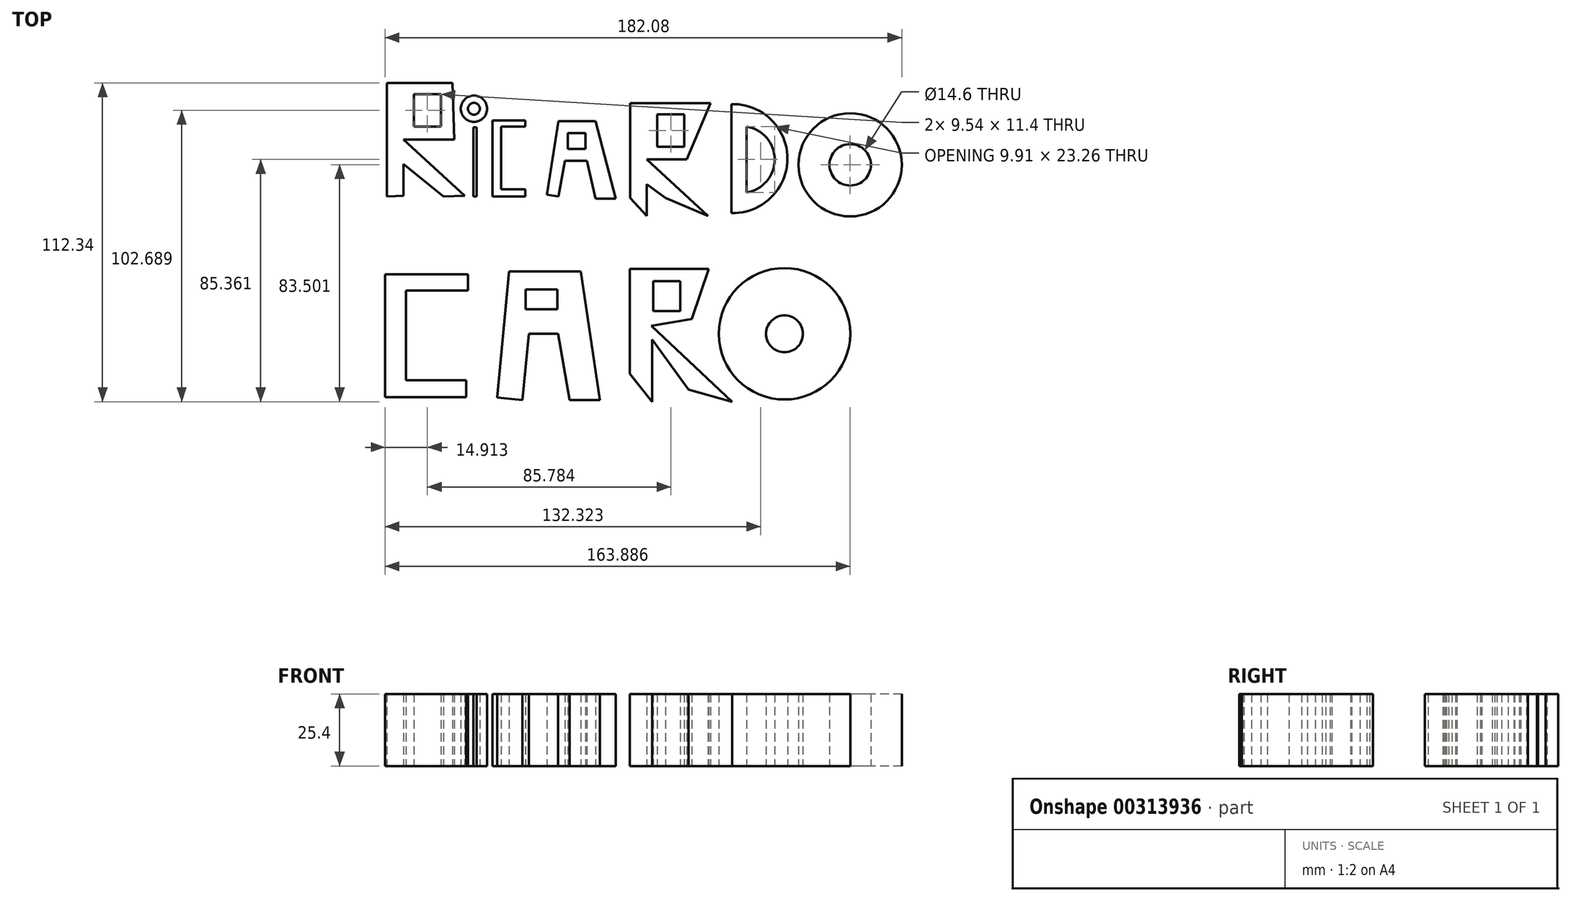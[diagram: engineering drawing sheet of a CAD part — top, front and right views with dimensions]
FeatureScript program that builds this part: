
annotation { "Feature Type Name" : "Feature", "Feature Type Description" : "" }
export const myFeature = defineFeature(function(context is Context, id is Id, definition is map)
    precondition{}
    {
        {
            var Q0;
            Q0=qCreatedBy(makeId("Top.planeOp"),FACE);
            var sketch = newSketch(context, id + "F0", { "sketchPlane" : qUnion([Q0])});
            skLineSegment(sketch, "E0", {"start": v(-68.38, 50.47) * mm, "end": v(-68.38, 10.47) * mm});
            skLineSegment(sketch, "E1", {"start": v(-68.38, 50.47) * mm, "end": v(-62.57, 50.47) * mm});
            skLineSegment(sketch, "E2", {"start": v(-62.57, 50.47) * mm, "end": v(-62.57, 10.7) * mm});
            skLineSegment(sketch, "E3", {"start": v(-68.38, 10.47) * mm, "end": v(-62.57, 10.7) * mm});
            skLineSegment(sketch, "E4", {"start": v(-62.57, 30.59) * mm, "end": v(-40.94, 10.7) * mm});
            skLineSegment(sketch, "E5", {"start": v(-62.57, 21.86) * mm, "end": v(-48.38, 10.47) * mm});
            skLineSegment(sketch, "E6", {"start": v(-48.38, 10.47) * mm, "end": v(-40.94, 10.7) * mm});
            skLineSegment(sketch, "E7", {"start": v(-62.57, 30.59) * mm, "end": v(-44.66, 30.59) * mm});
            skPoint(sketch, "E7.endSnap0", {"position": v(-44.66, 10.58) * mm});
            skLineSegment(sketch, "E8", {"start": v(-44.66, 30.59) * mm, "end": v(-45.28, 50.47) * mm});
            skLineSegment(sketch, "E9", {"start": v(-45.28, 50.47) * mm, "end": v(-62.57, 50.47) * mm});
            skLineSegment(sketch, "E10.bottom", {"start": v(-58.84, 46.52) * mm, "end": v(-49.3, 46.52) * mm});
            skLineSegment(sketch, "E10.top", {"start": v(-58.84, 35.12) * mm, "end": v(-49.3, 35.12) * mm});
            skLineSegment(sketch, "E10.left", {"start": v(-58.84, 46.52) * mm, "end": v(-58.84, 35.12) * mm});
            skLineSegment(sketch, "E10.right", {"start": v(-49.3, 46.52) * mm, "end": v(-49.3, 35.12) * mm});
            skLineSegment(sketch, "E11.bottom", {"start": v(-37.91, 34.89) * mm, "end": v(-36.75, 34.89) * mm});
            skLineSegment(sketch, "E11.top", {"start": v(-37.91, 10.47) * mm, "end": v(-36.75, 10.47) * mm});
            skLineSegment(sketch, "E11.left", {"start": v(-37.91, 34.89) * mm, "end": v(-37.91, 10.47) * mm});
            skLineSegment(sketch, "E11.right", {"start": v(-36.75, 34.89) * mm, "end": v(-36.75, 10.47) * mm});
            skPoint(sketch, "E12.oppositeSnap0", {"position": v(-54.08, 35.12) * mm});
            skLineSegment(sketch, "E12.bottom", {"start": v(-19.54, 37.21) * mm, "end": v(-31.17, 37.21) * mm});
            skLineSegment(sketch, "E12.top", {"start": v(-19.54, 35.12) * mm, "end": v(-31.17, 35.12) * mm});
            skLineSegment(sketch, "E12.left", {"start": v(-19.54, 37.21) * mm, "end": v(-19.54, 35.12) * mm});
            skLineSegment(sketch, "E12.right", {"start": v(-31.17, 37.21) * mm, "end": v(-31.17, 35.12) * mm});
            skLineSegment(sketch, "E13.bottom", {"start": v(-31.17, 37.21) * mm, "end": v(-28.14, 37.21) * mm});
            skLineSegment(sketch, "E13.top", {"start": v(-31.17, 10.47) * mm, "end": v(-28.14, 10.47) * mm});
            skLineSegment(sketch, "E13.left", {"start": v(-31.17, 37.21) * mm, "end": v(-31.17, 10.47) * mm});
            skLineSegment(sketch, "E13.right", {"start": v(-28.14, 37.21) * mm, "end": v(-28.14, 10.47) * mm});
            skLineSegment(sketch, "E14.bottom", {"start": v(-31.17, 10.47) * mm, "end": v(-19.54, 10.47) * mm});
            skLineSegment(sketch, "E14.top", {"start": v(-31.17, 13.02) * mm, "end": v(-19.54, 13.02) * mm});
            skLineSegment(sketch, "E14.left", {"start": v(-31.17, 10.47) * mm, "end": v(-31.17, 13.02) * mm});
            skLineSegment(sketch, "E14.right", {"start": v(-19.54, 10.47) * mm, "end": v(-19.54, 13.02) * mm});
            skLineSegment(sketch, "E15", {"start": v(-11.96, 11.1) * mm, "end": v(-7.9, 36.98) * mm});
            skLineSegment(sketch, "E16", {"start": v(-7.9, 36.98) * mm, "end": v(5.12, 36.98) * mm});
            skLineSegment(sketch, "E17", {"start": v(12.33, 9.77) * mm, "end": v(5.12, 9.77) * mm});
            skLineSegment(sketch, "E18", {"start": v(5.12, 9.77) * mm, "end": v(2.1, 23.03) * mm});
            skLineSegment(sketch, "E19", {"start": v(-11.96, 11.1) * mm, "end": v(-7.9, 10.47) * mm});
            skLineSegment(sketch, "E20", {"start": v(-7.9, 10.47) * mm, "end": v(-5.58, 23.03) * mm});
            skLineSegment(sketch, "E21", {"start": v(-5.58, 23.03) * mm, "end": v(2.1, 23.03) * mm});
            skLineSegment(sketch, "E22.bottom", {"start": v(-4.65, 32.8) * mm, "end": v(1.63, 32.8) * mm});
            skLineSegment(sketch, "E22.top", {"start": v(-4.65, 27.21) * mm, "end": v(1.63, 27.21) * mm});
            skLineSegment(sketch, "E22.left", {"start": v(-4.65, 32.8) * mm, "end": v(-4.65, 27.21) * mm});
            skLineSegment(sketch, "E22.right", {"start": v(1.63, 32.8) * mm, "end": v(1.63, 27.21) * mm});
            skCircle(sketch, "E23", {"center": v(-37.68, 41.4) * mm, "radius": 4.62 * mm});
            skCircle(sketch, "E24", {"center": v(-37.68, 41.4) * mm, "radius": 2.1 * mm});
            skLineSegment(sketch, "E25", {"start": v(17.4, 43.4) * mm, "end": v(17.4, 10) * mm});
            skLineSegment(sketch, "E26", {"start": v(17.4, 43.4) * mm, "end": v(23.22, 43.4) * mm});
            skLineSegment(sketch, "E27", {"start": v(23.22, 43.4) * mm, "end": v(23.22, 3.63) * mm});
            skLineSegment(sketch, "E28", {"start": v(17.4, 10) * mm, "end": v(23.22, 3.63) * mm});
            skLineSegment(sketch, "E29", {"start": v(23.22, 23.52) * mm, "end": v(44.85, 3.63) * mm});
            skLineSegment(sketch, "E30", {"start": v(23.22, 14.8) * mm, "end": v(29.77, 10) * mm});
            skLineSegment(sketch, "E31", {"start": v(29.77, 10) * mm, "end": v(44.85, 3.63) * mm});
            skLineSegment(sketch, "E32", {"start": v(23.22, 23.52) * mm, "end": v(37.3, 23.52) * mm});
            skPoint(sketch, "E32.endSnap0", {"position": v(37.3, 6.82) * mm});
            skLineSegment(sketch, "E33", {"start": v(37.3, 23.52) * mm, "end": v(45.7, 43.4) * mm});
            skLineSegment(sketch, "E34", {"start": v(45.7, 43.4) * mm, "end": v(23.22, 43.4) * mm});
            skLineSegment(sketch, "E35.bottom", {"start": v(26.94, 39.45) * mm, "end": v(36.48, 39.45) * mm});
            skLineSegment(sketch, "E35.top", {"start": v(26.94, 28.06) * mm, "end": v(36.48, 28.06) * mm});
            skLineSegment(sketch, "E35.left", {"start": v(26.94, 39.45) * mm, "end": v(26.94, 28.06) * mm});
            skLineSegment(sketch, "E35.right", {"start": v(36.48, 39.45) * mm, "end": v(36.48, 28.06) * mm});
            skPoint(sketch, "E36.oppositeSnap0", {"position": v(31.7, 28.06) * mm});
            skLineSegment(sketch, "E37", {"start": v(53.03, 43.03) * mm, "end": v(53.03, 4.65) * mm});
            skArc(sketch, "E38", {"start": v(53.03, 4.65) * mm, "mid": v(72.8, 23.84) * mm, "end": v(53.03, 43.03) * mm});
            skLineSegment(sketch, "E39", {"start": v(58.38, 35.12) * mm, "end": v(58.38, 11.86) * mm});
            skArc(sketch, "E40", {"start": v(58.38, 11.86) * mm, "mid": v(68.29, 23.5) * mm, "end": v(58.38, 35.12) * mm});
            skCircle(sketch, "E41", {"center": v(94.9, 21.63) * mm, "radius": 18.2 * mm});
            skCircle(sketch, "E42", {"center": v(94.9, 21.63) * mm, "radius": 7.3 * mm});
            skLineSegment(sketch, "E43", {"start": v(5.12, 36.98) * mm, "end": v(12.33, 9.77) * mm});
            skSolve(sketch);
        }
        {
            var Q0;
            Q0 = qSketchRegion(id + "F0", true);
            extrude(context, id + "F1", {"entities" : qUnion([Q0]), "depth" : 25.4 * mm});
        }
        {
            var Q0;
            Q0=qCreatedBy(makeId("Top.planeOp"),FACE);
            var sketch = newSketch(context, id + "F2", { "sketchPlane" : qUnion([Q0])});
            skLineSegment(sketch, "E44.bottom", {"start": v(-39.8, -16.91) * mm, "end": v(-68.99, -16.91) * mm});
            skLineSegment(sketch, "E44.top", {"start": v(-39.8, -22.7) * mm, "end": v(-68.99, -22.7) * mm});
            skLineSegment(sketch, "E44.left", {"start": v(-39.8, -16.91) * mm, "end": v(-39.8, -22.7) * mm});
            skLineSegment(sketch, "E44.right", {"start": v(-68.99, -16.91) * mm, "end": v(-68.99, -22.7) * mm});
            skLineSegment(sketch, "E45.bottom", {"start": v(-68.99, -16.91) * mm, "end": v(-61.57, -16.91) * mm});
            skLineSegment(sketch, "E45.top", {"start": v(-68.99, -60.24) * mm, "end": v(-61.57, -60.24) * mm});
            skLineSegment(sketch, "E45.left", {"start": v(-68.99, -16.91) * mm, "end": v(-68.99, -60.24) * mm});
            skLineSegment(sketch, "E45.right", {"start": v(-61.57, -16.91) * mm, "end": v(-61.57, -60.24) * mm});
            skLineSegment(sketch, "E46.bottom", {"start": v(-68.99, -60.24) * mm, "end": v(-40.4, -60.24) * mm});
            skLineSegment(sketch, "E46.top", {"start": v(-68.99, -54.33) * mm, "end": v(-40.4, -54.33) * mm});
            skLineSegment(sketch, "E46.left", {"start": v(-68.99, -60.24) * mm, "end": v(-68.99, -54.33) * mm});
            skLineSegment(sketch, "E46.right", {"start": v(-40.4, -60.24) * mm, "end": v(-40.4, -54.33) * mm});
            skLineSegment(sketch, "E47", {"start": v(-29.52, -60.44) * mm, "end": v(-25.25, -15.95) * mm});
            skLineSegment(sketch, "E48", {"start": v(-25.25, -15.95) * mm, "end": v(0, -15.95) * mm});
            skLineSegment(sketch, "E49", {"start": v(0, -15.95) * mm, "end": v(6.68, -61.3) * mm});
            skLineSegment(sketch, "E50", {"start": v(-29.52, -60.44) * mm, "end": v(-20.61, -61.3) * mm});
            skLineSegment(sketch, "E51", {"start": v(-20.61, -61.3) * mm, "end": v(-18.37, -37.9) * mm});
            skLineSegment(sketch, "E52", {"start": v(-18.37, -37.9) * mm, "end": v(-8.06, -37.9) * mm});
            skLineSegment(sketch, "E53", {"start": v(-8.06, -37.9) * mm, "end": v(-3.99, -61.3) * mm});
            skLineSegment(sketch, "E54", {"start": v(-3.99, -61.3) * mm, "end": v(6.68, -61.3) * mm});
            skLineSegment(sketch, "E55.bottom", {"start": v(-19.42, -22.28) * mm, "end": v(-8.25, -22.28) * mm});
            skLineSegment(sketch, "E55.top", {"start": v(-19.42, -29.28) * mm, "end": v(-8.25, -29.28) * mm});
            skLineSegment(sketch, "E55.left", {"start": v(-19.42, -22.28) * mm, "end": v(-19.42, -29.28) * mm});
            skLineSegment(sketch, "E55.right", {"start": v(-8.25, -22.28) * mm, "end": v(-8.25, -29.28) * mm});
            skLineSegment(sketch, "E56", {"start": v(17.2, -15.12) * mm, "end": v(17.2, -51.96) * mm});
            skLineSegment(sketch, "E57", {"start": v(17.2, -51.96) * mm, "end": v(25.07, -61.87) * mm});
            skLineSegment(sketch, "E58", {"start": v(25.07, -61.87) * mm, "end": v(25.07, -39.9) * mm});
            skLineSegment(sketch, "E59", {"start": v(25.07, -39.9) * mm, "end": v(37.9, -57.61) * mm});
            skLineSegment(sketch, "E60", {"start": v(53.27, -61.87) * mm, "end": v(24.9, -35.14) * mm});
            skLineSegment(sketch, "E61", {"start": v(17.2, -15.12) * mm, "end": v(45.08, -15.12) * mm});
            skLineSegment(sketch, "E62", {"start": v(45.08, -15.12) * mm, "end": v(39.04, -32.73) * mm});
            skLineSegment(sketch, "E63", {"start": v(39.04, -32.73) * mm, "end": v(24.9, -35.14) * mm});
            skLineSegment(sketch, "E64.bottom", {"start": v(25.44, -19.4) * mm, "end": v(35.07, -19.4) * mm});
            skLineSegment(sketch, "E64.top", {"start": v(25.44, -29.95) * mm, "end": v(35.07, -29.95) * mm});
            skLineSegment(sketch, "E64.left", {"start": v(25.44, -19.4) * mm, "end": v(25.44, -29.95) * mm});
            skLineSegment(sketch, "E64.right", {"start": v(35.07, -19.4) * mm, "end": v(35.07, -29.95) * mm});
            skCircle(sketch, "E65", {"center": v(71.75, -37.94) * mm, "radius": 23.16 * mm});
            skCircle(sketch, "E66", {"center": v(71.75, -37.94) * mm, "radius": 6.5 * mm});
            skLineSegment(sketch, "E67", {"start": v(53.27, -61.87) * mm, "end": v(37.9, -57.61) * mm});
            skSolve(sketch);
        }
        {
            var Q0;
            Q0 = qSketchRegion(id + "F2", true);
            extrude(context, id + "F3", {"entities" : qUnion([Q0]), "depth" : 25.4 * mm});
        }
    });
